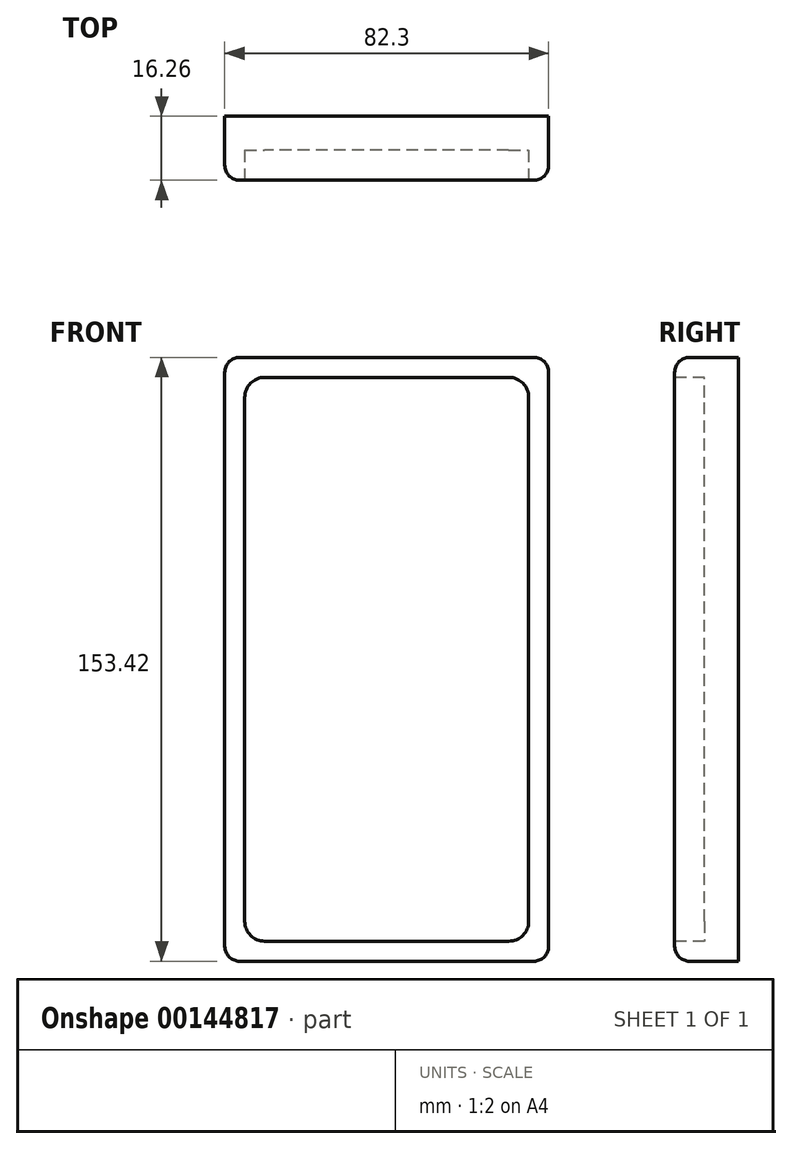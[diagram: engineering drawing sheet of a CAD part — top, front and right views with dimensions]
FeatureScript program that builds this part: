
annotation { "Feature Type Name" : "Feature", "Feature Type Description" : "" }
export const myFeature = defineFeature(function(context is Context, id is Id, definition is map)
    precondition{}
    {
        {
            var Q0;
            Q0=qCreatedBy(makeId("Front.planeOp"),FACE);
            var sketch = newSketch(context, id + "F0", { "sketchPlane" : qUnion([Q0])});
            skLineSegment(sketch, "E0.bottom", {"start": v(41.15, -76.7) * mm, "end": v(-41.15, -76.7) * mm});
            skLineSegment(sketch, "E0.top", {"start": v(41.15, 76.7) * mm, "end": v(-41.15, 76.7) * mm});
            skLineSegment(sketch, "E0.left", {"start": v(41.15, -76.7) * mm, "end": v(41.15, 76.7) * mm});
            skLineSegment(sketch, "E0.right", {"start": v(-41.15, -76.7) * mm, "end": v(-41.15, 76.7) * mm});
            skPoint(sketch, "E0.middle", {"position": v(0, 0) * mm});
            skSolve(sketch);
        }
        {
            var Q0;
            Q0=makeQuery(id+"F0.imprint","IMPRINT",FACE,{"disambiguationData":[TD([[makeQuery(id+"F0.imprint","IMPRINT",EDGE,{"derivedFrom":sQuery(id+"F0.wireOp",EDGE,"E0.bottom")}),-1.0]])]});
            extrude(context, id + "F1", {"entities" : qUnion([Q0]), "depth" : 16.26 * mm});
        }
        {
            var Q0;
            Q0=makeQuery(id+"F1.opExtrude","CAP_FACE",FACE,{"disambiguationData":[OSD([sQuery(id+"F0.wireOp",EDGE,"E0.bottom"),sQuery(id+"F0.wireOp",EDGE,"E0.top"),sQuery(id+"F0.wireOp",EDGE,"E0.left"),sQuery(id+"F0.wireOp",EDGE,"E0.right")])],"isStart":false});
            var sketch = newSketch(context, id + "F2", { "sketchPlane" : qUnion([Q0])});
            skLineSegment(sketch, "E1.bottom", {"start": v(36.07, -71.63) * mm, "end": v(-36.07, -71.63) * mm});
            skLineSegment(sketch, "E1.top", {"start": v(36.07, 71.63) * mm, "end": v(-36.07, 71.63) * mm});
            skLineSegment(sketch, "E1.left", {"start": v(36.07, -71.63) * mm, "end": v(36.07, 71.63) * mm});
            skLineSegment(sketch, "E1.right", {"start": v(-36.07, -71.63) * mm, "end": v(-36.07, 71.63) * mm});
            skPoint(sketch, "E1.middle", {"position": v(0, 0) * mm});
            skSolve(sketch);
        }
        {
            var Q0;
            Q0 = qSketchRegion(id + "F2", true);
            extrude(context, id + "F3", {"entities" : qUnion([Q0]), "operationType" : NewBodyOperationType.REMOVE, "oppositeDirection" : true, "depth" : 7.62 * mm});
        }
        {
            var Q0;
            Q0=makeQuery(id+"F3.boolean.opBoolean","COPY",EDGE,{"derivedFrom":makeQuery(id+"F3.opExtrude","SWEPT_EDGE",EDGE,{"disambiguationData":[OSD([sQuery(id+"F2.wireOp",EDGE,"E1.top"),sQuery(id+"F2.wireOp",EDGE,"E1.right")])]})});
            fillet(context, id + "F4", {"entities" : qUnion([Q0]), "radius" : 5.08 * mm, "tangentPropagation" : true, "allowEdgeOverflow" : false});
        }
        {
            var Q0;
            Q0=makeQuery(id+"F3.boolean.opBoolean","COPY",EDGE,{"derivedFrom":makeQuery(id+"F3.opExtrude","SWEPT_EDGE",EDGE,{"disambiguationData":[OSD([sQuery(id+"F2.wireOp",EDGE,"E1.top"),sQuery(id+"F2.wireOp",EDGE,"E1.left")])]})});
            fillet(context, id + "F5", {"entities" : qUnion([Q0]), "radius" : 5.08 * mm, "tangentPropagation" : true, "allowEdgeOverflow" : false});
        }
        {
            var Q0;
            Q0=makeQuery(id+"F3.boolean.opBoolean","COPY",EDGE,{"derivedFrom":makeQuery(id+"F3.opExtrude","SWEPT_EDGE",EDGE,{"disambiguationData":[OSD([sQuery(id+"F2.wireOp",EDGE,"E1.bottom"),sQuery(id+"F2.wireOp",EDGE,"E1.left")])]})});
            fillet(context, id + "F6", {"entities" : qUnion([Q0]), "radius" : 5.08 * mm, "tangentPropagation" : true, "allowEdgeOverflow" : false});
        }
        {
            var Q0;
            Q0=makeQuery(id+"F3.boolean.opBoolean","COPY",EDGE,{"derivedFrom":makeQuery(id+"F3.opExtrude","SWEPT_EDGE",EDGE,{"disambiguationData":[OSD([sQuery(id+"F2.wireOp",EDGE,"E1.bottom"),sQuery(id+"F2.wireOp",EDGE,"E1.right")])]})});
            fillet(context, id + "F7", {"entities" : qUnion([Q0]), "radius" : 5.08 * mm, "tangentPropagation" : true, "allowEdgeOverflow" : false});
        }
        {
            var Q0;
            Q0=makeQuery(id+"F1.opExtrude","CAP_EDGE",EDGE,{"disambiguationData":[OSD([sQuery(id+"F0.wireOp",EDGE,"E0.left")])],"isStart":false});
            var Q1;
            Q1=makeQuery(id+"F1.opExtrude","CAP_EDGE",EDGE,{"disambiguationData":[OSD([sQuery(id+"F0.wireOp",EDGE,"E0.right")])],"isStart":false});
            fillet(context, id + "F8", {"entities" : qUnion([Q0, Q1]), "radius" : 3.8 * mm, "tangentPropagation" : true, "allowEdgeOverflow" : false});
        }
        {
            var Q0;
            Q0=makeQuery(id+"F1.opExtrude","CAP_EDGE",EDGE,{"disambiguationData":[OSD([sQuery(id+"F0.wireOp",EDGE,"E0.top")])],"isStart":false});
            var Q1;
            Q1=makeQuery(id+"F1.opExtrude","CAP_EDGE",EDGE,{"disambiguationData":[OSD([sQuery(id+"F0.wireOp",EDGE,"E0.bottom")])],"isStart":false});
            fillet(context, id + "F9", {"entities" : qUnion([Q0, Q1]), "radius" : 3.8 * mm, "tangentPropagation" : true, "allowEdgeOverflow" : false});
        }
    });
